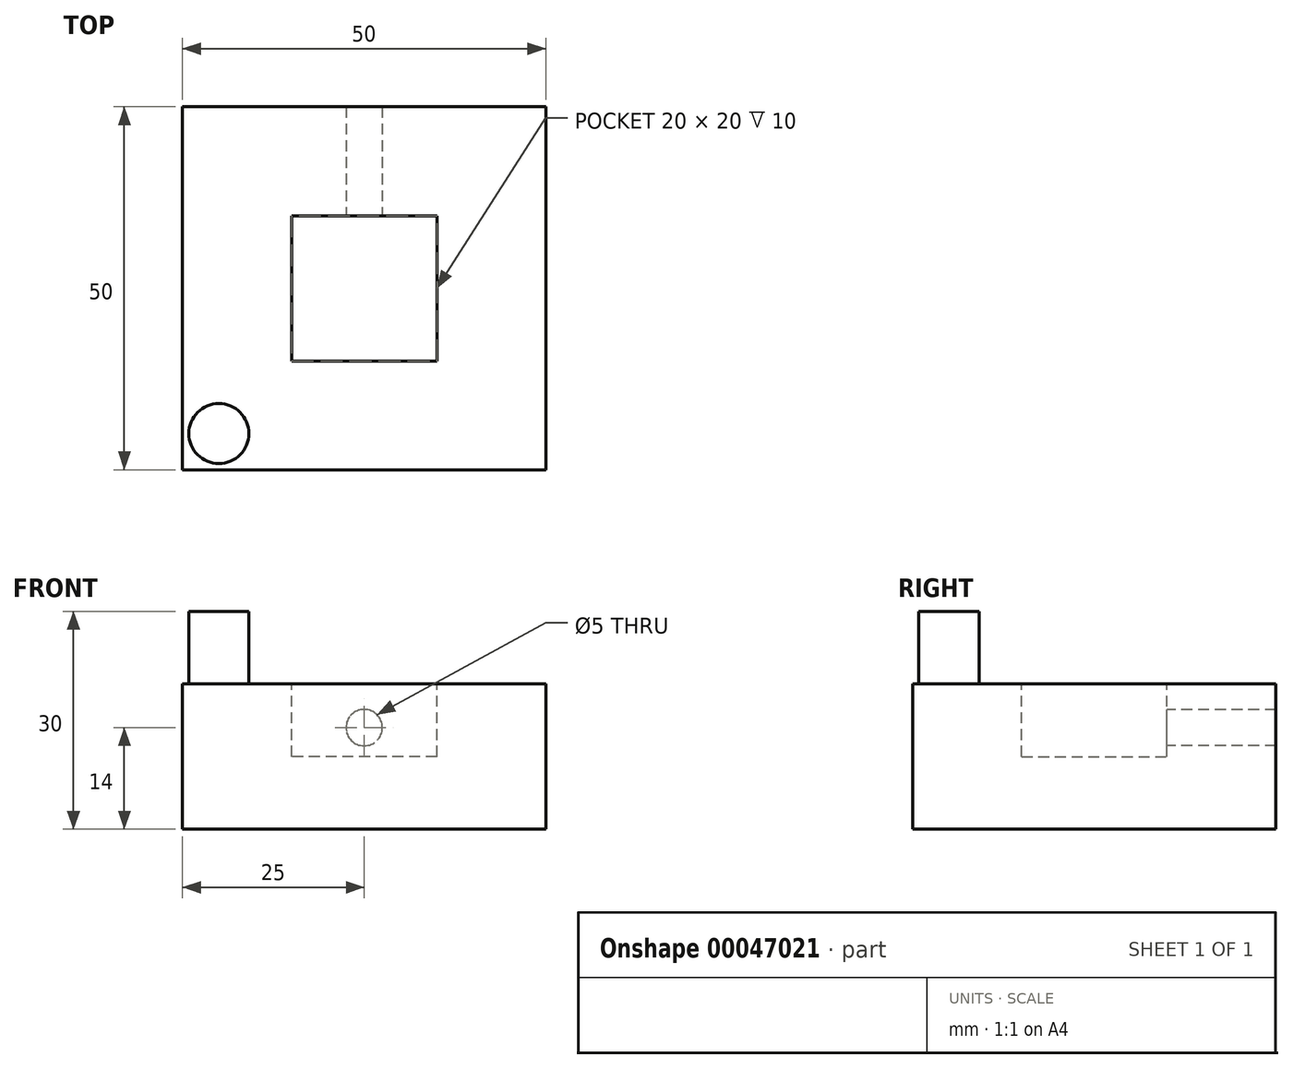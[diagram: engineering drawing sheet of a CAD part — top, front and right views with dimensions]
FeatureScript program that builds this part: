
annotation { "Feature Type Name" : "Feature", "Feature Type Description" : "" }
export const myFeature = defineFeature(function(context is Context, id is Id, definition is map)
    precondition{}
    {
        {
            var Q0;
            Q0=qCreatedBy(makeId("Top.planeOp"),FACE);
            var sketch = newSketch(context, id + "F0", { "sketchPlane" : qUnion([Q0])});
            skLineSegment(sketch, "E0.rect.bottom", {"start": v(-25, -25) * mm, "end": v(25, -25) * mm});
            skLineSegment(sketch, "E0.rect.top", {"start": v(-25, 25) * mm, "end": v(25, 25) * mm});
            skLineSegment(sketch, "E0.rect.left", {"start": v(-25, -25) * mm, "end": v(-25, 25) * mm});
            skLineSegment(sketch, "E0.rect.right", {"start": v(25, -25) * mm, "end": v(25, 25) * mm});
            skPoint(sketch, "E0.rect.middle", {"position": v(0, 0) * mm});
            skSolve(sketch);
        }
        {
            var Q0;
            Q0=makeQuery(id+"F0.imprint","IMPRINT",FACE,{"disambiguationData":[TD([[makeQuery(id+"F0.imprint","IMPRINT",EDGE,{"derivedFrom":sQuery(id+"F0.wireOp",EDGE,"E0.rect.bottom")}),1.0]])]});
            extrude(context, id + "F1", {"entities" : qUnion([Q0]), "depth" : 20 * mm});
        }
        {
            var Q0;
            Q0=makeQuery(id+"F1.opExtrude","CAP_FACE",FACE,{"disambiguationData":[OSD([sQuery(id+"F0.wireOp",EDGE,"E0.rect.bottom"),sQuery(id+"F0.wireOp",EDGE,"E0.rect.top"),sQuery(id+"F0.wireOp",EDGE,"E0.rect.left"),sQuery(id+"F0.wireOp",EDGE,"E0.rect.right")])],"isStart":false});
            var sketch = newSketch(context, id + "F2", { "sketchPlane" : qUnion([Q0])});
            skLineSegment(sketch, "E1.rect.bottom", {"start": v(10, -10) * mm, "end": v(-10, -10) * mm});
            skLineSegment(sketch, "E1.rect.top", {"start": v(10, 10) * mm, "end": v(-10, 10) * mm});
            skLineSegment(sketch, "E1.rect.left", {"start": v(10, -10) * mm, "end": v(10, 10) * mm});
            skLineSegment(sketch, "E1.rect.right", {"start": v(-10, -10) * mm, "end": v(-10, 10) * mm});
            skPoint(sketch, "E1.rect.middle", {"position": v(0, 0) * mm});
            skSolve(sketch);
        }
        {
            var Q0;
            Q0=makeQuery(id+"F2.imprint","IMPRINT",FACE,{"disambiguationData":[TD([[makeQuery(id+"F2.imprint","IMPRINT",EDGE,{"derivedFrom":sQuery(id+"F2.wireOp",EDGE,"E1.rect.bottom")}),-1.0]])]});
            extrude(context, id + "F3", {"entities" : qUnion([Q0]), "operationType" : NewBodyOperationType.REMOVE, "oppositeDirection" : true, "depth" : 10 * mm});
        }
        {
            var Q0;
            Q0=makeQuery(id+"F1.opExtrude","CAP_FACE",FACE,{"disambiguationData":[OSD([sQuery(id+"F0.wireOp",EDGE,"E0.rect.bottom"),sQuery(id+"F0.wireOp",EDGE,"E0.rect.top"),sQuery(id+"F0.wireOp",EDGE,"E0.rect.left"),sQuery(id+"F0.wireOp",EDGE,"E0.rect.right")])],"isStart":false});
            var sketch = newSketch(context, id + "F4", { "sketchPlane" : qUnion([Q0])});
            skCircle(sketch, "E2", {"center": v(-20, -20) * mm, "radius": 4.14 * mm});
            skSolve(sketch);
        }
        {
            var Q0;
            Q0=makeQuery(id+"F4.imprint","IMPRINT",FACE,{"disambiguationData":[TD([[makeQuery(id+"F4.imprint","IMPRINT",EDGE,{"derivedFrom":sQuery(id+"F4.wireOp",EDGE,"E2")}),1.0]])]});
            extrude(context, id + "F5", {"entities" : qUnion([Q0]), "operationType" : NewBodyOperationType.ADD, "depth" : 10 * mm});
        }
        {
            var Q0;
            Q0=makeQuery(id+"F3.boolean.opBoolean","COPY",FACE,{"derivedFrom":makeQuery(id+"F3.opExtrude","SWEPT_FACE",FACE,{"disambiguationData":[OSD([sQuery(id+"F2.wireOp",EDGE,"E1.rect.top")])]})});
            var sketch = newSketch(context, id + "F6", { "sketchPlane" : qUnion([Q0])});
            skCircle(sketch, "E3", {"center": v(0, 14) * mm, "radius": 2.5 * mm});
            skSolve(sketch);
        }
        {
            var Q0;
            Q0=makeQuery(id+"F6.imprint","IMPRINT",FACE,{"disambiguationData":[TD([[makeQuery(id+"F6.imprint","IMPRINT",EDGE,{"derivedFrom":sQuery(id+"F6.wireOp",EDGE,"E3")}),1.0]])]});
            extrude(context, id + "F7", {"entities" : qUnion([Q0]), "operationType" : NewBodyOperationType.REMOVE, "oppositeDirection" : true, "depth" : 24.56 * mm});
        }
    });
